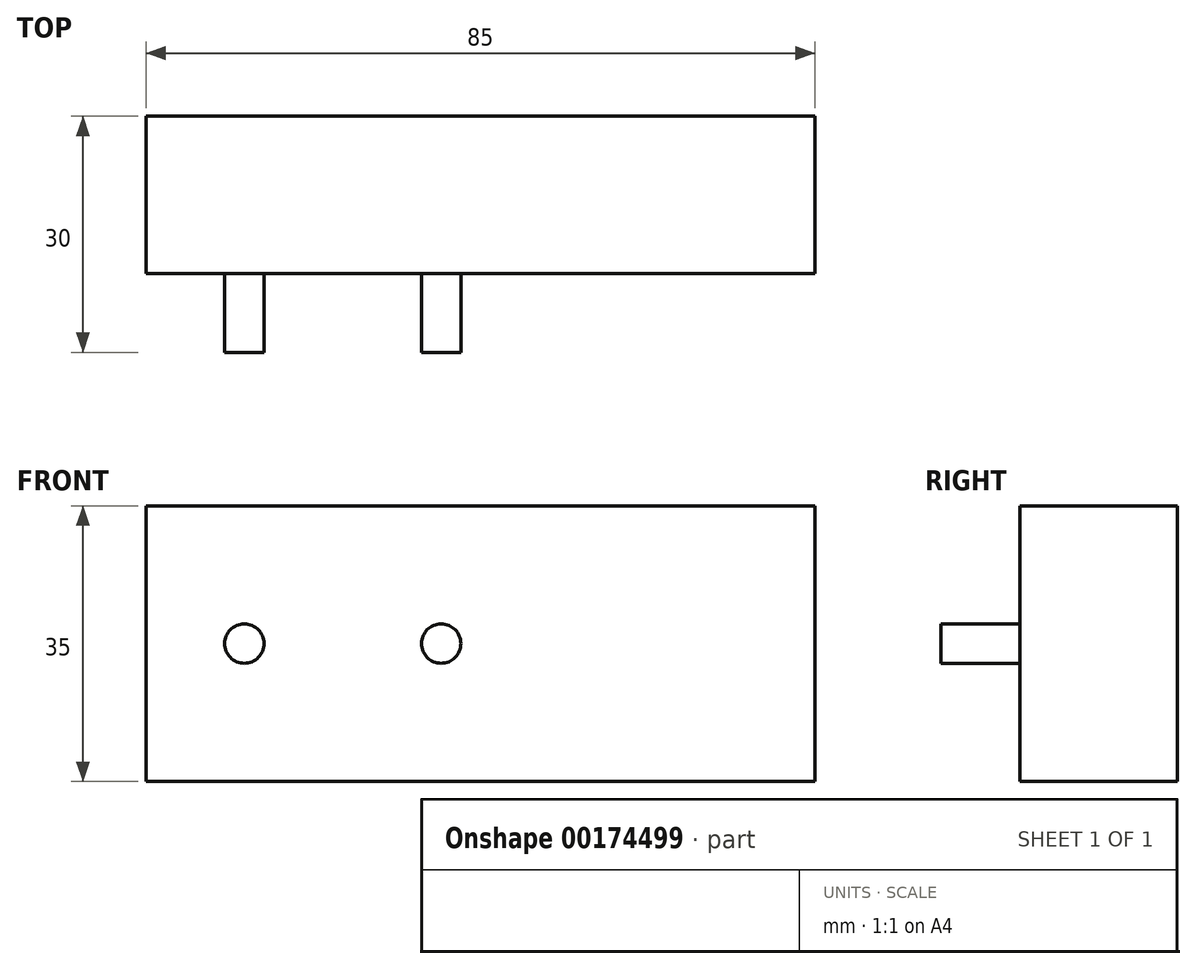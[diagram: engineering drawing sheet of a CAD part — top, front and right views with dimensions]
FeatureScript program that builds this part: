
annotation { "Feature Type Name" : "Feature", "Feature Type Description" : "" }
export const myFeature = defineFeature(function(context is Context, id is Id, definition is map)
    precondition{}
    {
        {
            var Q0;
            Q0=qCreatedBy(makeId("Front.planeOp"),FACE);
            var sketch = newSketch(context, id + "F0", { "sketchPlane" : qUnion([Q0])});
            skLineSegment(sketch, "E0.bottom", {"start": v(42.5, -17.5) * mm, "end": v(-42.5, -17.5) * mm});
            skLineSegment(sketch, "E0.top", {"start": v(42.5, 17.5) * mm, "end": v(-42.5, 17.5) * mm});
            skLineSegment(sketch, "E0.left", {"start": v(42.5, -17.5) * mm, "end": v(42.5, 17.5) * mm});
            skLineSegment(sketch, "E0.right", {"start": v(-42.5, -17.5) * mm, "end": v(-42.5, 17.5) * mm});
            skPoint(sketch, "E0.middle", {"position": v(0, 0) * mm});
            skSolve(sketch);
        }
        {
            var Q0;
            Q0=makeQuery(id+"F0.imprint","IMPRINT",FACE,{"disambiguationData":[TD([[makeQuery(id+"F0.imprint","IMPRINT",EDGE,{"derivedFrom":sQuery(id+"F0.wireOp",EDGE,"E0.bottom")}),-1.0]])]});
            extrude(context, id + "F1", {"entities" : qUnion([Q0]), "oppositeDirection" : true, "depth" : 20 * mm});
        }
        {
            var Q0;
            Q0=makeQuery(id+"F1.opExtrude","CAP_FACE",FACE,{"disambiguationData":[OSD([sQuery(id+"F0.wireOp",EDGE,"E0.bottom"),sQuery(id+"F0.wireOp",EDGE,"E0.top"),sQuery(id+"F0.wireOp",EDGE,"E0.left"),sQuery(id+"F0.wireOp",EDGE,"E0.right")])],"isStart":true});
            var sketch = newSketch(context, id + "F2", { "sketchPlane" : qUnion([Q0])});
            skCircle(sketch, "E1", {"center": v(-5, 0) * mm, "radius": 2.5 * mm});
            skCircle(sketch, "E2", {"center": v(-30, 0) * mm, "radius": 2.5 * mm});
            skSolve(sketch);
        }
        {
            var Q0;
            Q0=makeQuery(id+"F2.imprint","IMPRINT",FACE,{"disambiguationData":[TD([[makeQuery(id+"F2.imprint","IMPRINT",EDGE,{"derivedFrom":sQuery(id+"F2.wireOp",EDGE,"E2")}),1.0]])]});
            var Q1;
            Q1=makeQuery(id+"F2.imprint","IMPRINT",FACE,{"disambiguationData":[TD([[makeQuery(id+"F2.imprint","IMPRINT",EDGE,{"derivedFrom":sQuery(id+"F2.wireOp",EDGE,"E1")}),1.0]])]});
            extrude(context, id + "F3", {"entities" : qUnion([Q0, Q1]), "operationType" : NewBodyOperationType.ADD, "depth" : 10 * mm});
        }
    });
